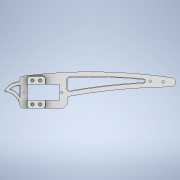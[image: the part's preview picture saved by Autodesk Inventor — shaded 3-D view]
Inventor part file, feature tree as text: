
AUTODESK INVENTOR PART (.ipt)
format: ipt  version: 2020.3 (Build 243373000, 373)  size: 425,984 bytes
history: native  units: mm
features: fillet x9, hole x4, plane x3, extrude x2, sketch x1, chamfer x1
ambient origin geometry x8: Origin, YZ Plane, XZ Plane, XY Plane, X Axis, Y Axis, Z Axis, Center Point
bodies: Solid1 (feature_tree)
feature tree (20):
  sketch  "Sketch1"  dims[d4=6.0mm d5=24.6mm d6=12.4mm d7=6.0mm d15=7.0mm d17=9.0mm d21=20.0mm d23=80.0mm d24=20.0mm d29=29.670597mm d30=6.0mm d31=10.0mm d33=6.0mm d34=0.0mm d40=3.0mm d41=3.0mm d42=2.0mm d43=4.0mm d44=3.0mm d45=4.0mm d50=13.0mm d51=12.0mm d52=22.68928mm d54=1.9mm d55=50.8mm d56=4.0mm d57=2.0mm d58=90.0deg d59=8.0mm d60=20.594885mm d61=0.5mm d62=2.2mm d63=4.0mm d64=4.0mm d65=2.0mm d66=90.0deg d67=8.0mm d68=20.594885mm d69=20.92mm d70=0.0mm d71=2.0mm d80=3.0mm d81=2.0mm d82=45.0deg d87=0.5mm d88=0.5mm d89=6.8mm d90=28.4mm d99=3.0mm d100=6.0mm d101=4.0mm d102=2.0mm d103=90.0deg d104=4.3mm d105=0.0mm d107=420.0mm d108=4.0mm d109=4.0mm d110=6.0mm d111=2.0mm d112=2.0mm d113=0.5mm d114=2.1mm d115=6.0mm d116=4.0mm d117=2.0mm d118=90.0deg d119=7.3mm d120=0.0mm d121=90.0deg d122=90.0deg d123=-7.5mm]
  extrude  "Extrusion1"  Depth=7.3mm
  fillet  "Fillet1"  Radius=12.4mm
  fillet  "Fillet2"  Radius=6.0mm
  fillet  "Fillet3"  Radius=7.0mm
  hole  "Hole1"  [1 undecoded]
  fillet  "Fillet4"  Radius=20.0mm
  hole  "Hole2"  [1 undecoded]
  extrude  "Extrusion3"  Depth=7.3mm
  hole  "Hole5"  [1 undecoded]
  fillet  "Fillet5"  Radius=6.0mm
  chamfer  "Chamfer2"  Distance=10.0mm
  fillet  "Fillet8"  Radius=6.0mm
  fillet  "Fillet10"  Radius=3.0mm
  fillet  "Fillet9"  Radius=3.0mm
  fillet  "Fillet11"  Radius=2.0mm
  hole  "Hole6"  [1 undecoded]
  plane  "Work Plane1"
  plane  "Work Plane2"
  plane  "Work Plane3"
note: 4 required parameter values undecoded (feature->parameter linkage not recoverable at this tier; creation-order binding heuristic only, values carry confidence <= 0.55)
